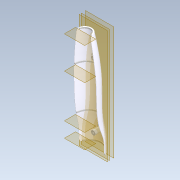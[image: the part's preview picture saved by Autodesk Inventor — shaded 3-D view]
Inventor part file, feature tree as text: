
AUTODESK INVENTOR PART (.ipt)
format: ipt  version: 2020.2 (Build 242310000, 310)  size: 528,384 bytes
history: native  units: mm
features: sketch x13, extrude x8, plane x7, loft x1, fillet x1, chamfer x1
ambient origin geometry x8: Origin, YZ Plane, XZ Plane, XY Plane, X Axis, Y Axis, Z Axis, Center Point
bodies: Solid1 (feature_tree)
feature tree (31):
  plane  "Work Plane1"
  plane  "Work Plane2"
  plane  "Work Plane3"
  plane  "Work Plane4"
  loft  "Loft1"
  fillet  "Fillet1"  Radius=35.0mm
  plane  "Work Plane5"
  extrude  "Extrusion1"  Depth=100.0mm
  extrude  "Extrusion2"  Depth=1.0mm
  plane  "Work Plane7"
  extrude  "Extrusion3"  Depth=1.0mm
  plane  "Work Plane8"
  extrude  "Extrusion4"  Depth=5.0mm
  extrude  "rib1"  Depth=30.0mm
  extrude  "rib2"  TaperAngle=90.0deg  [1 undecoded]
  extrude  "rib3"  Depth=10.0mm
  extrude  "rib4"  Depth=3.0mm
  chamfer  "Chamfer1"  Distance=21.746mm
  sketch  "Sketch1"  dims[d5=30.0mm d7=210.0mm d9=35.0mm]
  sketch  "Sketch2"  dims[d11=0.0mm d12=90.0deg d13=0.0mm d14=90.0deg d15=0.0mm d16=90.0deg d17=0.0mm d18=90.0deg d19=100.0mm]
  sketch  "Sketch3"  dims[d21=0.0mm d22=90.0deg d25=1.0mm]
  sketch  "Sketch4"  dims[d26=1.0mm d27=1.0mm]
  sketch  "Sketch5"  dims[d28=1.0mm d29=5.0mm]
  sketch  "Sketch6"  dims[d30=-20.0mm d31=30.0mm]
  sketch  "Sketch7"  dims[d32=150.0mm d33=90.0deg]
  sketch  "Sketch8"  dims[d34=10.0mm d35=10.0mm]
  sketch  "Sketch9"  dims[d36=21.746mm d37=0.0mm d38=3.0mm]
  sketch  "Sketch10"  dims[d39=3.0mm d40=21.746mm d41=0.0mm]
  sketch  "Sketch11"  dims[d42=-5.0mm]
  sketch  "Sketch12"  dims[d43=7.0mm]
  sketch  "Sketch13"  dims[d44=10.0mm d45=0.0mm d46=-15.0mm d47=7.0mm d48=36.746mm d49=0.0mm d51=2.0mm d52=3.0mm d53=0.0mm d55=2.0mm d56=3.0mm d57=0.0mm d59=2.0mm d60=3.0mm d61=0.0mm d63=2.0mm d64=3.0mm d65=0.0mm d66=4.0mm d67=2.0mm d68=45.0deg]
note: 1 required parameter value undecoded (feature->parameter linkage not recoverable at this tier; creation-order binding heuristic only, values carry confidence <= 0.55)
